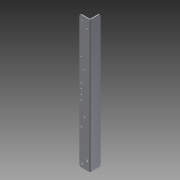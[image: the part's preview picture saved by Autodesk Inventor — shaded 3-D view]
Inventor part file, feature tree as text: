
AUTODESK INVENTOR PART (.ipt)
format: ipt  version: 2014 SP1 (Build 180222100, 222)  size: 262,144 bytes
history: native  units: in
note: dims shown in document units (in); Inventor stores cm internally (conversion verified against a paired STEP export)
features: other x5, sketch x4, sheet_metal_op x2, reference x2, chamfer x1
ambient origin geometry x8: Origin, YZ Plane, XZ Plane, XY Plane, X Axis, Y Axis, Z Axis, Center Point
bodies: Solid1 (feature_tree)
feature tree (14):
  sketch  "Sketch1"  dims[d0=20.0in]
  sheet_metal_op  "Face1"
  sheet_metal_op  "Fold1"
  chamfer  "Corner Round1"
  other  "Plate1"
  sketch  "Sketch2"  dims[d1=3.0in]
  sketch  "Sketch3"  dims[d2=1.5in]
  reference  "Reference1"
  reference  "Reference2"
  sketch  "Sketch4"  dims[d3=0.25in d4=0.01in d5=0.25in d6=11.811in d8=0.6638in d9=0.3937in d11=1.0in d13=0.125in d14=0.125in d15=0.0625in d16=0.25in d17=0.125in d18=90.0deg d19=0.05in d20=0.313in d22=0.75in d23=0.313in d24=0.313in d25=0.375in d26=0.75in d27=0.75in d28=0.55in d29=0.125in d30=0.0in d31=6.2008in d32=0.266in d34=0.266in d36=1.5748in d38=0.75in d39=0.3937in d41=1.0in d43=0.25in d44=0.125in d45=0.0in d46=0.25in d47=0.875in d48=0.875in d49=1.5in d50=4.7244in d52=1.5455in d53=0.3937in d55=1.0in d57=0.266in d58=0.266in d59=0.25in d60=9.25in d61=0.125in d62=0.0in]
  other  "Cut1"
  other  "Cut2"
  other  "Cut3"
  other  "Definition1"
